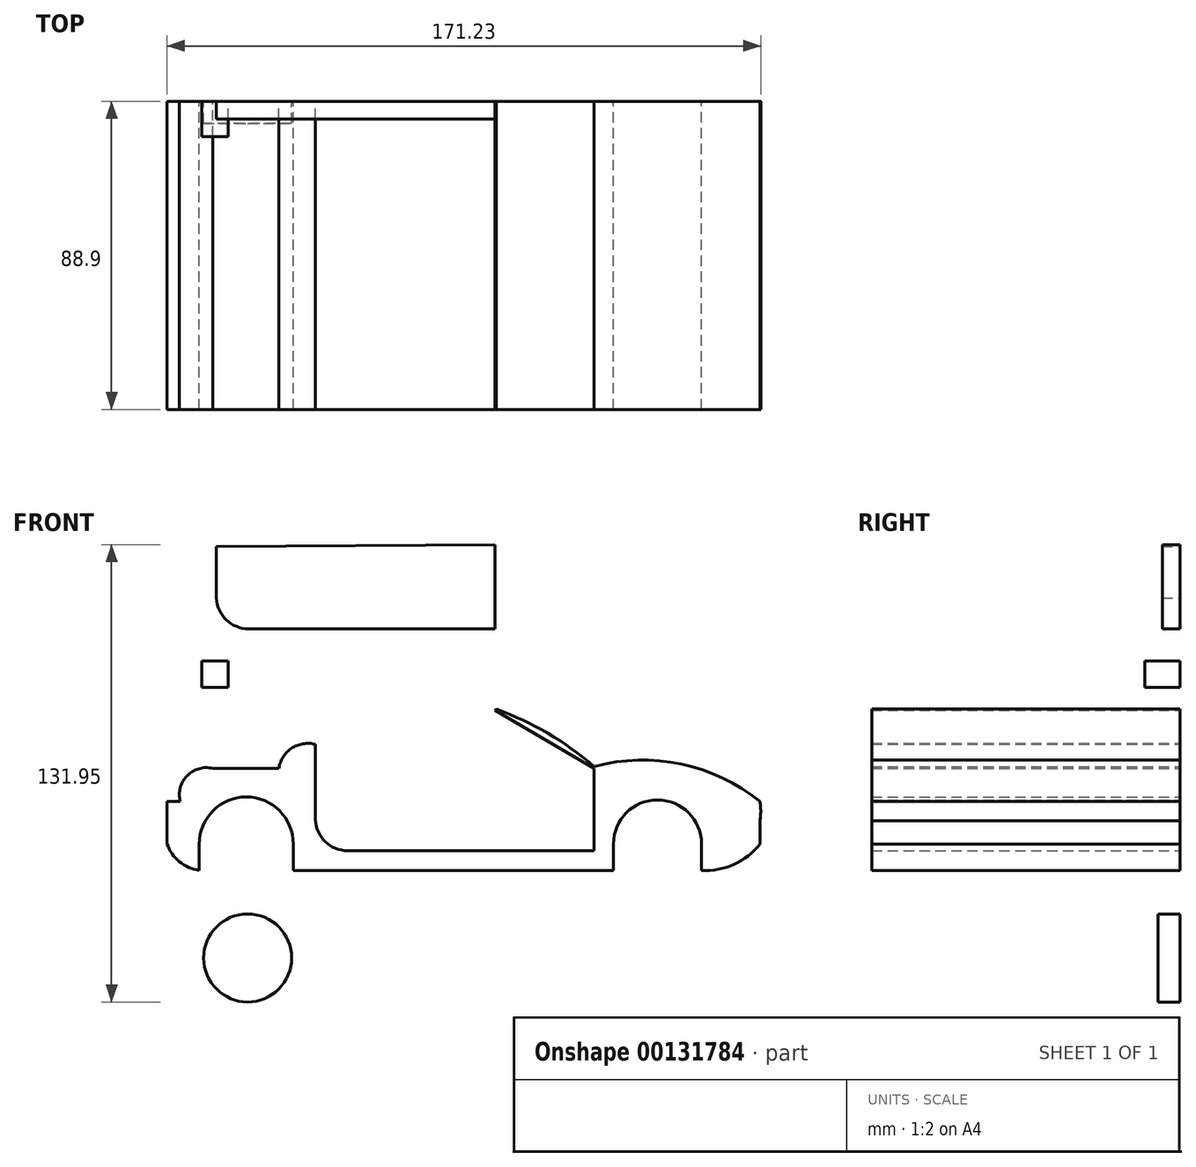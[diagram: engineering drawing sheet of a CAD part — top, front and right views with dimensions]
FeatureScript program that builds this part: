
annotation { "Feature Type Name" : "Feature", "Feature Type Description" : "" }
export const myFeature = defineFeature(function(context is Context, id is Id, definition is map)
    precondition{}
    {
        {
            var Q0;
            Q0=qCreatedBy(makeId("Front.planeOp"),FACE);
            var sketch = newSketch(context, id + "F0", { "sketchPlane" : qUnion([Q0])});
            skLineSegment(sketch, "E0", {"start": v(-73.12, -19.87) * mm, "end": v(-73.12, -12.25) * mm});
            skLineSegment(sketch, "E1", {"start": v(-46, -12.25) * mm, "end": v(-46, -19.87) * mm});
            skArc(sketch, "E2", {"start": v(-46, -12.25) * mm, "mid": v(-59.55, 1.31) * mm, "end": v(-73.12, -12.25) * mm});
            skArc(sketch, "E3", {"start": v(-82.38, -12.25) * mm, "mid": v(-78.81, -17.36) * mm, "end": v(-73.12, -19.87) * mm});
            skLineSegment(sketch, "E4", {"start": v(-82.38, -12.25) * mm, "end": v(-82.38, 0) * mm});
            skArc(sketch, "E5", {"start": v(-71.47, 9.52) * mm, "mid": v(-72.04, 9.58) * mm, "end": v(-72.6, 9.6) * mm});
            skLineSegment(sketch, "E6", {"start": v(-39.64, 9.52) * mm, "end": v(-39.64, 16.48) * mm});
            skLineSegment(sketch, "E7", {"start": v(-39.64, 9.52) * mm, "end": v(-39.64, -5.29) * mm});
            skPoint(sketch, "E8.orphan", {"position": v(-39.64, -14.2) * mm});
            skLineSegment(sketch, "E9", {"start": v(-30.32, -14.2) * mm, "end": v(40.8, -14.2) * mm});
            skLineSegment(sketch, "E10", {"start": v(46.36, -12.25) * mm, "end": v(46.36, -19.87) * mm});
            skLineSegment(sketch, "E11", {"start": v(46.36, -19.87) * mm, "end": v(46.36, -12.25) * mm});
            skLineSegment(sketch, "E12", {"start": v(71.76, -12.25) * mm, "end": v(71.76, -19.87) * mm});
            skArc(sketch, "E13", {"start": v(71.76, -12.25) * mm, "mid": v(59.06, 0.45) * mm, "end": v(46.36, -12.25) * mm});
            skPoint(sketch, "E14.end.orphan", {"position": v(40.8, 9.52) * mm});
            skLineSegment(sketch, "E15", {"start": v(40.8, -14.2) * mm, "end": v(40.8, 10.1) * mm});
            skLineSegment(sketch, "E16", {"start": v(40.8, 9.52) * mm, "end": v(12.15, 26.32) * mm});
            skLineSegment(sketch, "E17", {"start": v(12.59, 26.65) * mm, "end": v(12.15, 26.32) * mm});
            skArc(sketch, "E18", {"start": v(88.62, -5.57) * mm, "mid": v(88.85, -2.79) * mm, "end": v(88.62, 0) * mm});
            skArc(sketch, "E19", {"start": v(88.62, 0) * mm, "mid": v(65.91, 10.75) * mm, "end": v(40.8, 10.1) * mm});
            skPoint(sketch, "E20.end.orphan", {"position": v(99.88, 0) * mm});
            skPoint(sketch, "E21.end.orphan", {"position": v(99.88, -12.25) * mm});
            skLineSegment(sketch, "E22", {"start": v(88.62, 0) * mm, "end": v(88.62, -12.25) * mm});
            skArc(sketch, "E23", {"start": v(71.76, -19.87) * mm, "mid": v(81.14, -18.16) * mm, "end": v(88.62, -12.25) * mm});
            skArc(sketch, "E24", {"start": v(-39.64, -5.29) * mm, "mid": v(-36.77, -11.61) * mm, "end": v(-30.32, -14.2) * mm});
            skLineSegment(sketch, "E25", {"start": v(-46, -19.87) * mm, "end": v(46.36, -19.87) * mm});
            skPoint(sketch, "E26.end.orphan", {"position": v(-46, 9.52) * mm});
            skLineSegment(sketch, "E27", {"start": v(-71.47, 9.52) * mm, "end": v(-39.64, 9.52) * mm});
            skArc(sketch, "E28", {"start": v(-39.64, 16.48) * mm, "mid": v(-46.46, 15.35) * mm, "end": v(-50.17, 9.52) * mm});
            skArc(sketch, "E29", {"start": v(40.8, 10.1) * mm, "mid": v(27.43, 19.63) * mm, "end": v(12.59, 26.65) * mm});
            skLineSegment(sketch, "E30", {"start": v(-78.57, 0) * mm, "end": v(-82.38, 0) * mm});
            skArc(sketch, "E31", {"start": v(-69.2, 9.52) * mm, "mid": v(-76.61, 7.44) * mm, "end": v(-78.57, 0) * mm});
            skSolve(sketch);
        }
        {
            var Q0;
            Q0 = qSketchRegion(id + "F0", true);
            extrude(context, id + "F1", {"entities" : qUnion([Q0]), "depth" : 88.9 * mm});
        }
        {
            var Q0;
            Q0=qCreatedBy(makeId("Front.planeOp"),FACE);
            var sketch = newSketch(context, id + "F2", { "sketchPlane" : qUnion([Q0])});
            skLineSegment(sketch, "E32", {"start": v(-68.2, 73.52) * mm, "end": v(-68.2, 58.71) * mm});
            skLineSegment(sketch, "E33", {"start": v(-58.89, 49.8) * mm, "end": v(12.23, 49.8) * mm});
            skLineSegment(sketch, "E34", {"start": v(12.23, 49.8) * mm, "end": v(12.23, 74.1) * mm});
            skArc(sketch, "E35", {"start": v(-68.2, 58.71) * mm, "mid": v(-65.33, 52.39) * mm, "end": v(-58.89, 49.8) * mm});
            skLineSegment(sketch, "E36", {"start": v(-68.2, 73.52) * mm, "end": v(12.23, 74.1) * mm});
            skSolve(sketch);
        }
        {
            var Q0;
            Q0 = qSketchRegion(id + "F2", true);
            extrude(context, id + "F3", {"entities" : qUnion([Q0]), "depth" : 5.08 * mm});
        }
        {
            var Q0;
            Q0=qCreatedBy(makeId("Front.planeOp"),FACE);
            var sketch = newSketch(context, id + "F4", { "sketchPlane" : qUnion([Q0])});
            skCircle(sketch, "E37", {"center": v(-59.15, -45.15) * mm, "radius": 12.7 * mm});
            skSolve(sketch);
        }
        {
            var Q0;
            Q0 = qSketchRegion(id + "F4", true);
            extrude(context, id + "F5", {"entities" : qUnion([Q0]), "depth" : 6.35 * mm});
        }
        {
            var Q0;
            Q0=qCreatedBy(makeId("Front.planeOp"),FACE);
            var sketch = newSketch(context, id + "F6", { "sketchPlane" : qUnion([Q0])});
            skLineSegment(sketch, "E38.bottom", {"start": v(-72.44, 40.48) * mm, "end": v(-64.82, 40.48) * mm});
            skLineSegment(sketch, "E38.top", {"start": v(-72.44, 32.86) * mm, "end": v(-64.82, 32.86) * mm});
            skLineSegment(sketch, "E38.left", {"start": v(-72.44, 40.48) * mm, "end": v(-72.44, 32.86) * mm});
            skLineSegment(sketch, "E38.right", {"start": v(-64.82, 40.48) * mm, "end": v(-64.82, 32.86) * mm});
            skSolve(sketch);
        }
        {
            var Q0;
            Q0 = qSketchRegion(id + "F6", true);
            extrude(context, id + "F7", {"entities" : qUnion([Q0]), "depth" : 10.16 * mm});
        }
    });
